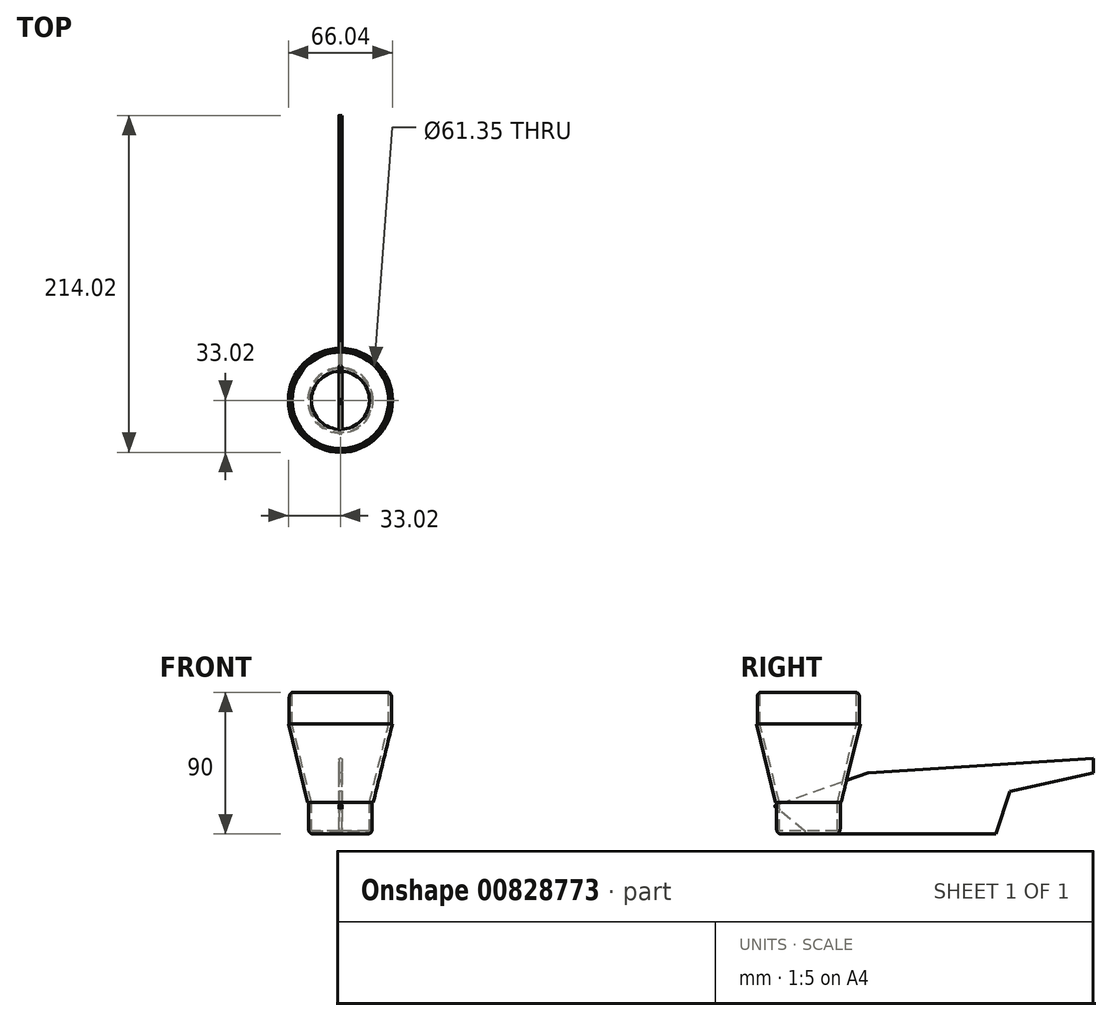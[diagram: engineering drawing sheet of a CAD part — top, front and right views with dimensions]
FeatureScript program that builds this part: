
annotation { "Feature Type Name" : "Feature", "Feature Type Description" : "" }
export const myFeature = defineFeature(function(context is Context, id is Id, definition is map)
    precondition{}
    {
        {
            var Q0;
            Q0=qCreatedBy(makeId("Right.planeOp"),FACE);
            var sketch = newSketch(context, id + "F0", { "sketchPlane" : qUnion([Q0])});
            skLineSegment(sketch, "E0", {"start": v(0, 0) * mm, "end": v(-22, 18) * mm});
            skLineSegment(sketch, "E1", {"start": v(-22, 18) * mm, "end": v(38, 39) * mm});
            skLineSegment(sketch, "E2", {"start": v(38, 39) * mm, "end": v(181, 48) * mm});
            skLineSegment(sketch, "E3", {"start": v(181, 48) * mm, "end": v(181, 39) * mm});
            skLineSegment(sketch, "E4", {"start": v(181, 39) * mm, "end": v(128, 27) * mm});
            skLineSegment(sketch, "E5", {"start": v(128, 27) * mm, "end": v(119, 0) * mm});
            skLineSegment(sketch, "E6", {"start": v(119, 0) * mm, "end": v(0, 0) * mm});
            skSolve(sketch);
        }
        {
            var Q0;
            Q0=makeQuery(id+"F0.imprint","IMPRINT",FACE,{"disambiguationData":[TD([[makeQuery(id+"F0.imprint","IMPRINT",EDGE,{"derivedFrom":sQuery(id+"F0.wireOp",EDGE,"E0")}),-1.0]])]});
            extrude(context, id + "F1", {"entities" : qUnion([Q0]), "endBound" : BoundingType.SYMMETRIC, "depth" : 2 * mm, "offsetDistance" : 25 * mm});
        }
        {
            var Q0;
            Q0=makeQuery(id+"F1.opExtrude","CAP_EDGE",EDGE,{"disambiguationData":[OSD([sQuery(id+"F0.wireOp",EDGE,"E2")])],"isStart":false});
            var Q1;
            Q1=makeQuery(id+"F1.opExtrude","CAP_EDGE",EDGE,{"disambiguationData":[OSD([sQuery(id+"F0.wireOp",EDGE,"E2")])],"isStart":true});
            fillet(context, id + "F2", {"entities" : qUnion([Q0, Q1]), "radius" : 0.62 * mm, "tangentPropagation" : true, "allowEdgeOverflow" : false});
        }
        {
            var Q0;
            Q0=makeQuery(id+"F1.opExtrude","CAP_EDGE",EDGE,{"disambiguationData":[OSD([sQuery(id+"F0.wireOp",EDGE,"E1")])],"isStart":true});
            var Q1;
            Q1=makeQuery(id+"F1.opExtrude","CAP_EDGE",EDGE,{"disambiguationData":[OSD([sQuery(id+"F0.wireOp",EDGE,"E1")])],"isStart":false});
            fillet(context, id + "F3", {"entities" : qUnion([Q0, Q1]), "radius" : 0.62 * mm, "tangentPropagation" : true, "allowEdgeOverflow" : false});
        }
        {
            var Q0;
            Q0=makeQuery(id+"F1.opExtrude","CAP_EDGE",EDGE,{"disambiguationData":[OSD([sQuery(id+"F0.wireOp",EDGE,"E0")])],"isStart":false});
            var Q1;
            Q1=makeQuery(id+"F1.opExtrude","CAP_EDGE",EDGE,{"disambiguationData":[OSD([sQuery(id+"F0.wireOp",EDGE,"E0")])],"isStart":true});
            fillet(context, id + "F4", {"entities" : qUnion([Q0, Q1]), "radius" : 0.62 * mm, "tangentPropagation" : true, "allowEdgeOverflow" : false});
        }
        {
            var Q0;
            Q0=qCreatedBy(makeId("Front.planeOp"),FACE);
            var sketch = newSketch(context, id + "F5", { "sketchPlane" : qUnion([Q0])});
            skLineSegment(sketch, "E7", {"start": v(0, 49.48) * mm, "end": v(0, -51.3) * mm, "construction": true});
            skLineSegment(sketch, "E8", {"start": v(30.67, 90) * mm, "end": v(30.67, 70) * mm});
            skLineSegment(sketch, "E9", {"start": v(30.67, 70) * mm, "end": v(33.02, 70) * mm});
            skLineSegment(sketch, "E10", {"start": v(18.43, 20) * mm, "end": v(18.43, 0) * mm});
            skLineSegment(sketch, "E11", {"start": v(20.79, 20) * mm, "end": v(18.43, 20) * mm});
            skLineSegment(sketch, "E12", {"start": v(30.67, 70) * mm, "end": v(18.43, 20) * mm});
            skLineSegment(sketch, "E13", {"start": v(33.02, 70) * mm, "end": v(20.79, 20) * mm});
            skLineSegment(sketch, "E14", {"start": v(20.23, 20) * mm, "end": v(20.23, 0) * mm});
            skLineSegment(sketch, "E15", {"start": v(18.43, 0) * mm, "end": v(20.23, 0) * mm});
            skLineSegment(sketch, "E16", {"start": v(30.67, 90) * mm, "end": v(32.47, 90) * mm});
            skLineSegment(sketch, "E17", {"start": v(32.47, 90) * mm, "end": v(32.47, 70) * mm});
            skSolve(sketch);
        }
        {
            var Q0;
            Q0=makeQuery(id+"F5.imprint","IMPRINT",FACE,{"disambiguationData":[TD([[makeQuery(id+"F5.imprint","IMPRINT",EDGE,{"derivedFrom":sQuery(id+"F5.wireOp",EDGE,"E9")}),-1.0]])]});
            var Q1;
            Q1=makeQuery(id+"F5.imprint","IMPRINT",FACE,{"disambiguationData":[TD([[makeQuery(id+"F5.imprint","IMPRINT",EDGE,{"derivedFrom":sQuery(id+"F5.wireOp",EDGE,"E10")}),1.0]])]});
            var Q2;
            {var subQ0=sQuery(id+"F5.wireOp",EDGE,"E8");Q2=makeQuery(id+"F5.imprint","IMPRINT",FACE,{"disambiguationData":[TD([[makeQuery(id+"F5.imprint","IMPRINT",EDGE,{"derivedFrom":subQ0}),1.0]])]});}
            var Q3;
            Q3=sQuery(id+"F5.wireOp",EDGE,"E7");
            revolve(context, id + "F6", {"surfaceOperationType" : NewSurfaceOperationType.NEW, "entities" : qUnion([Q0, Q1, Q2]), "axis" : qUnion([Q3]), "revolveType" : RevolveType.FULL});
        }
        {
            var Q0;
            Q0=qCreatedBy(makeId("Top.planeOp"),FACE);
            var sketch = newSketch(context, id + "F7", { "sketchPlane" : qUnion([Q0])});
            skCircle(sketch, "E18.0", {"center": v(0, 0) * mm, "radius": 18.43 * mm});
            skSolve(sketch);
        }
        {
            var Q0;
            Q0 = qSketchRegion(id + "F7", true);
            extrude(context, id + "F8", {"entities" : qUnion([Q0]), "operationType" : NewBodyOperationType.ADD, "depth" : 2 * mm, "offsetDistance" : 25 * mm});
        }
        {
            var Q0;
            Q0=makeQuery(id+"F6.opRevolve","SWEPT_EDGE",EDGE,{"disambiguationData":[OSD([sQuery(id+"F5.wireOp",EDGE,"MRoH7HAg-zSln-37fb-V0PF-GjUkU9aArLeH"),sQuery(id+"F5.wireOp",EDGE,"BEQjLZKC-yAqG-PHVs-0nXX-UHXcnk07M7Br")])]});
            var Q1;
            Q1=makeQuery(id+"F6.opRevolve","SWEPT_EDGE",EDGE,{"disambiguationData":[OSD([sQuery(id+"F5.wireOp",EDGE,"E14"),sQuery(id+"F5.wireOp",EDGE,"E15")])]});
            fillet(context, id + "F9", {"entities" : qUnion([Q0, Q1]), "radius" : 3.17 * mm, "tangentPropagation" : true, "allowEdgeOverflow" : false});
        }
        {
            var Q0;
            Q0=makeQuery(id+"F6.opRevolve","SWEPT_EDGE",EDGE,{"disambiguationData":[OSD([sQuery(id+"F5.wireOp",EDGE,"E16"),sQuery(id+"F5.wireOp",EDGE,"E17")])]});
            fillet(context, id + "F10", {"entities" : qUnion([Q0]), "radius" : 3.17 * mm, "tangentPropagation" : true, "allowEdgeOverflow" : false});
        }
    });
